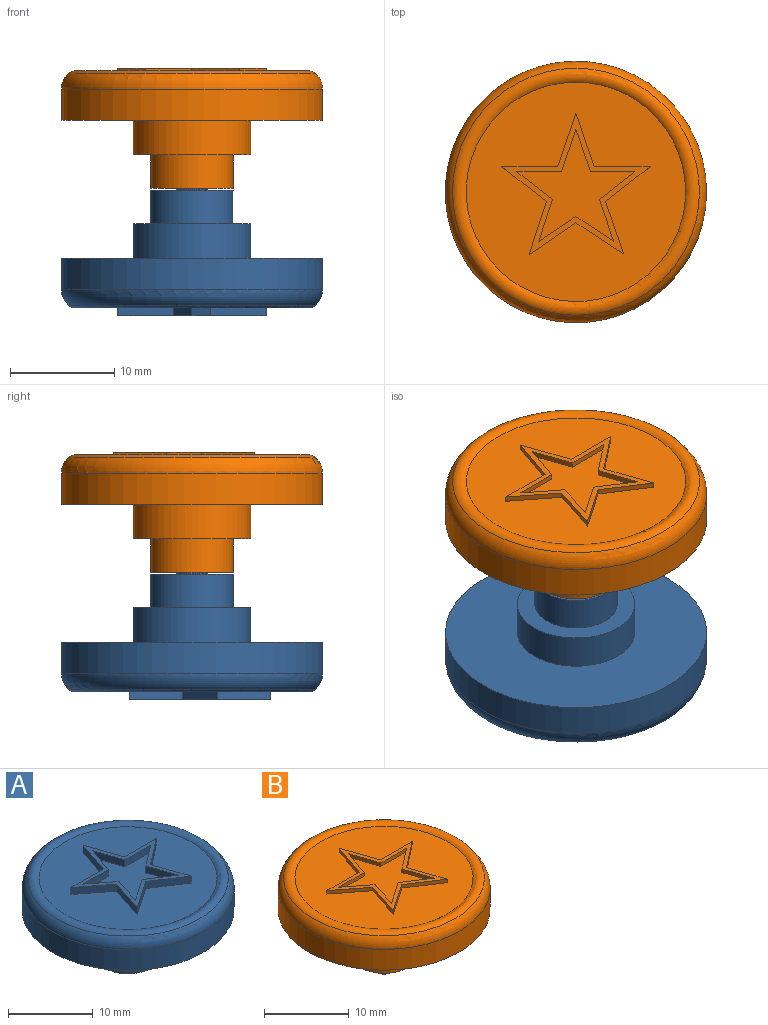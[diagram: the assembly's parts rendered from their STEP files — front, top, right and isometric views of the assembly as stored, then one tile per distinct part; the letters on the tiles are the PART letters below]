
ASSEMBLY  parts=2 mates=1
PART A: 34 faces, bbox 27.1x27.1x12.1 mm
  f0: cylinder r=12.5mm len=25mm, axis (0,0,-1), area 235.6mm2, adj f1,f6
  f1: plane 25x25mm, normal (0,0,-1), area 391.5mm2, adj f0,f2
  f2: cylinder r=5.62mm len=11.25mm, axis (0,0,1), area 116.6mm2, adj f1,f3
  f3: plane 11.25x11.25mm, normal (0,0,-1), area 50.4mm2, adj f2,f4
  f4: cylinder r=3.95mm len=7.9mm, axis (0,0,1), area 79.4mm2, adj f3,f5
  f5: plane 7.9x7.9mm, normal (0,0,-1), area 41.9mm2, adj f4,f31
  f6: torus R=10.5mm, axis (0,0,1), area 130.7mm2, adj f0,f8
  f7: plane 21x21mm, normal (0,0,1), area 280.7mm2, adj f8,f9,f10,f11,f12,f13,f14,f15
  f8: torus R=11.16mm, axis (0,0,-1), area 101.4mm2, adj f6,f7
  f9: plane 5.09x1.75mm, normal (-0.95,0.33,0), area 5.4mm2, adj f7,f10,f28,f29
  f10: plane 5.35x1mm, normal (0,1,0), area 5.4mm2, adj f7,f9,f11,f29
  f11: plane 4.27x3.33mm, normal (-0.61,-0.79,0), area 5.4mm2, adj f7,f10,f12,f29
  f12: plane 5.09x1.65mm, normal (-0.95,0.31,0), area 5.4mm2, adj f7,f11,f13,f29
  f13: plane 4.49x3.03mm, normal (0.56,-0.83,0), area 5.4mm2, adj f7,f12,f14,f29
  f14: plane 4.56x2.98mm, normal (-0.55,-0.84,0), area 5.4mm2, adj f7,f13,f15,f29
  f15: plane 5.03x1.73mm, normal (0.95,0.33,0), area 5.3mm2, adj f7,f14,f16,f29
  f16: plane 4.27x3.33mm, normal (0.61,-0.79,0), area 5.4mm2, adj f7,f15,f17,f29
  f17: plane 5.35x1mm, normal (0,1,0), area 5.4mm2, adj f7,f16,f28,f29
  f18: plane 4.25x1mm, normal (0,-1,0), area 4.3mm2, adj f19,f27,f29,f30
  f19: plane 4.05x1.39mm, normal (0.95,-0.33,0), area 4.3mm2, adj f18,f20,f29,f30
  f20: plane 4.05x1.39mm, normal (-0.95,-0.33,0), area 4.3mm2, adj f19,f21,f29,f30
  f21: plane 4.25x1mm, normal (0,-1,0), area 4.3mm2, adj f20,f22,f29,f30
  f22: plane 3.41x2.65mm, normal (-0.61,0.79,0), area 4.3mm2, adj f21,f23,f29,f30
  f23: plane 3.99x1.37mm, normal (-0.95,-0.33,0), area 4.2mm2, adj f22,f24,f29,f30
  f24: plane 3.62x2.36mm, normal (0.55,0.84,0), area 4.3mm2, adj f23,f25,f29,f30
  f25: plane 3.56x2.4mm, normal (-0.56,0.83,0), area 4.3mm2, adj f24,f26,f29,f30
  f26: plane 4.04x1.31mm, normal (0.95,-0.31,0), area 4.2mm2, adj f25,f27,f29,f30
  f27: plane 3.4x2.65mm, normal (0.61,0.79,0), area 4.3mm2, adj f18,f26,f29,f30
  f28: plane 5.09x1.75mm, normal (0.95,0.33,0), area 5.4mm2, adj f7,f9,f17,f29
  f29: plane 14.21x13.51mm, normal (0,0,1), area 24.2mm2, adj f9,f10,f11,f12,f13,f14,f15,f16
  f30: plane 11.3x10.74mm, normal (0,0,1), area 41.5mm2, adj f18,f19,f20,f21,f22,f23,f24,f25
  f31: cylinder r=1.5mm len=3mm, axis (0,0,1), area 0.9mm2, adj f5,f32
  f32: cone r=1.5mm half-angle=10deg, axis (0,0,-1), area 16.9mm2, adj f31,f33
  f33: plane 2.29x2.29mm, normal (0,0,-1), area 4.1mm2, adj f32
PART B: 34 faces, bbox 27.1x27.1x13.6 mm
  f0: cylinder r=12.5mm len=25mm, axis (0,0,-1), area 235.6mm2, adj f1,f6
  f1: plane 25x25mm, normal (0,0,-1), area 391.5mm2, adj f0,f2
  f2: cylinder r=5.62mm len=11.25mm, axis (0,0,1), area 116.6mm2, adj f1,f3
  f3: plane 11.25x11.25mm, normal (0,0,-1), area 50.4mm2, adj f2,f4
  f4: cylinder r=3.95mm len=7.9mm, axis (0,0,1), area 79.4mm2, adj f3,f5
  f5: plane 7.9x7.9mm, normal (0,0,-1), area 41.9mm2, adj f4,f31
  f6: torus R=10.5mm, axis (0,0,1), area 130.7mm2, adj f0,f8
  f7: plane 21x21mm, normal (0,0,1), area 280.7mm2, adj f8,f9,f10,f11,f12,f13,f14,f15
  f8: torus R=11.16mm, axis (0,0,-1), area 101.4mm2, adj f6,f7
  f9: plane 5.09x1.75mm, normal (-0.95,0.33,0), area 2.7mm2, adj f7,f10,f28,f29
  f10: plane 5.35x0.5mm, normal (0,1,0), area 2.7mm2, adj f7,f9,f11,f29
  f11: plane 4.27x3.33mm, normal (-0.61,-0.79,0), area 2.7mm2, adj f7,f10,f12,f29
  f12: plane 5.09x1.65mm, normal (-0.95,0.31,0), area 2.7mm2, adj f7,f11,f13,f29
  f13: plane 4.49x3.03mm, normal (0.56,-0.83,0), area 2.7mm2, adj f7,f12,f14,f29
  f14: plane 4.56x2.98mm, normal (-0.55,-0.84,0), area 2.7mm2, adj f7,f13,f15,f29
  f15: plane 5.03x1.73mm, normal (0.95,0.33,0), area 2.7mm2, adj f7,f14,f16,f29
  f16: plane 4.27x3.33mm, normal (0.61,-0.79,0), area 2.7mm2, adj f7,f15,f17,f29
  f17: plane 5.35x0.5mm, normal (0,1,0), area 2.7mm2, adj f7,f16,f28,f29
  f18: plane 4.25x0.5mm, normal (0,-1,0), area 2.1mm2, adj f19,f27,f29,f30
  f19: plane 4.05x1.39mm, normal (0.95,-0.33,0), area 2.1mm2, adj f18,f20,f29,f30
  f20: plane 4.05x1.39mm, normal (-0.95,-0.33,0), area 2.1mm2, adj f19,f21,f29,f30
  f21: plane 4.25x0.5mm, normal (0,-1,0), area 2.1mm2, adj f20,f22,f29,f30
  f22: plane 3.41x2.65mm, normal (-0.61,0.79,0), area 2.2mm2, adj f21,f23,f29,f30
  f23: plane 3.99x1.37mm, normal (-0.95,-0.33,0), area 2.1mm2, adj f22,f24,f29,f30
  f24: plane 3.62x2.36mm, normal (0.55,0.84,0), area 2.2mm2, adj f23,f25,f29,f30
  f25: plane 3.56x2.4mm, normal (-0.56,0.83,0), area 2.1mm2, adj f24,f26,f29,f30
  f26: plane 4.04x1.31mm, normal (0.95,-0.31,0), area 2.1mm2, adj f25,f27,f29,f30
  f27: plane 3.4x2.65mm, normal (0.61,0.79,0), area 2.2mm2, adj f18,f26,f29,f30
  f28: plane 5.09x1.75mm, normal (0.95,0.33,0), area 2.7mm2, adj f7,f9,f17,f29
  f29: plane 14.21x13.51mm, normal (0,0,1), area 24.2mm2, adj f9,f10,f11,f12,f13,f14,f15,f16
  f30: plane 11.3x10.74mm, normal (0,0,1), area 41.5mm2, adj f18,f19,f20,f21,f22,f23,f24,f25
  f31: cylinder r=1.5mm len=3mm, axis (0,0,1), area 0.9mm2, adj f5,f32
  f32: cone r=1.5mm half-angle=10deg, axis (0,0,1), area 16.9mm2, adj f31,f33
  f33: plane 2.29x2.29mm, normal (0,0,-1), area 4.1mm2, adj f32
PLACE A rot(axis=(1,0,0),180deg) t=(19.27,10.01,-15.34)mm
PLACE B t=(19.27,10.01,-2.14)mm
MATE fastened A.f31 <-> B.f31  axis (0,0,1) through (19.27,10.01,-10.74)mm
